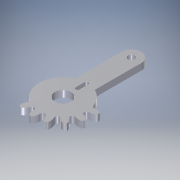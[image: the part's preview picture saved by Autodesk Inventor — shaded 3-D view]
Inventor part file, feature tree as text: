
AUTODESK INVENTOR PART (.ipt)
format: ipt  version: 2016 (Build 200138000, 138)  size: 450,048 bytes
history: native  units: mm
features: sketch x8, extrude x8, fillet x2, pattern_circular x1
ambient origin geometry x8: Origin, YZ Plane, XZ Plane, XY Plane, X Axis, Y Axis, Z Axis, Center Point
bodies: Solid1 (feature_tree)
feature tree (19):
  sketch  "Sketch1"  dims[d0=3.0mm d1=0.0mm]
  extrude  "Extrusion1"  TaperAngle=0.0deg  [1 undecoded]
  extrude  "Extrusion2"  Depth=10.0mm
  fillet  "Fillet1"  Radius=150.0mm
  pattern_circular  "Circular Pattern1"  Count=4  [1 undecoded]
  sketch  "Sketch3"  dims[d2=10.0mm d3=0.0mm d4=0.2mm d5=150.0mm d6=360.0deg]
  sketch  "Sketch4"  dims[d38=3.0mm]
  extrude  "Extrusion8"  Depth=10.0mm
  extrude  "Extrusion9"  Depth=4.5mm
  extrude  "Extrusion11"  Depth=10.0mm TaperAngle=0.0deg
  fillet  "Fillet8"  Radius=1.7mm
  extrude  "Extrusion12"  Depth=10.0mm TaperAngle=0.0deg
  extrude  "Extrusion13"  [1 undecoded]
  extrude  "Extrusion14"  [1 undecoded]
  sketch  "Sketch9"  dims[d39=35.6mm d40=0.0mm]
  sketch  "Sketch10"  dims[d41=7.51mm d42=40.0mm d43=0.0mm]
  sketch  "Sketch13"  dims[d52=10.0mm d53=0.0mm d54=3.0mm]
  sketch  "Sketch14"  dims[d55=31.1mm d56=4.5mm]
  sketch  "Sketch15"  dims[d57=10.0mm d58=0.0mm d59=10.0mm d60=0.0mm d62=1.7mm d64=10.0mm d65=0.0mm]
note: 4 required parameter values undecoded (feature->parameter linkage not recoverable at this tier; creation-order binding heuristic only, values carry confidence <= 0.55)
